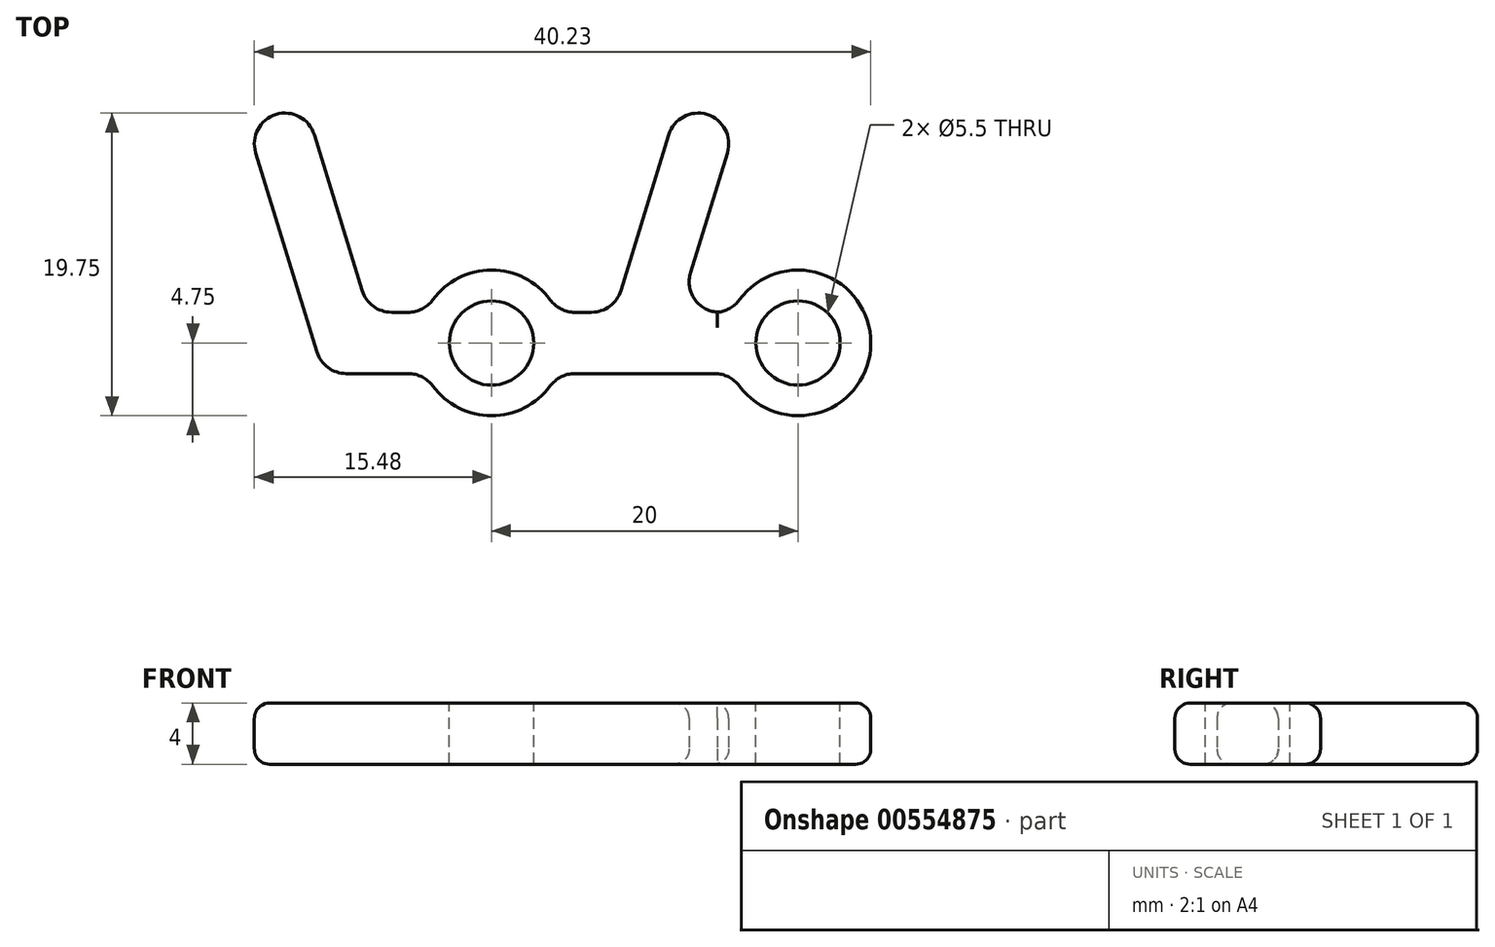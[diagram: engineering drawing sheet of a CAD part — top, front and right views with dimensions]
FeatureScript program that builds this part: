
annotation { "Feature Type Name" : "Feature", "Feature Type Description" : "" }
export const myFeature = defineFeature(function(context is Context, id is Id, definition is map)
    precondition{}
    {
        {
            var Q0;
            Q0=qCreatedBy(makeId("Top.planeOp"),FACE);
            var sketch = newSketch(context, id + "F0", { "sketchPlane" : qUnion([Q0])});
            skArc(sketch, "E0", {"start": v(-4.3, -2) * mm, "mid": v(0, -4.75) * mm, "end": v(4.3, -2) * mm});
            skLineSegment(sketch, "E1", {"start": v(4.3, -2) * mm, "end": v(10.95, -2) * mm});
            skLineSegment(sketch, "E2", {"start": v(12.19, 2) * mm, "end": v(16.19, 15) * mm});
            skLineSegment(sketch, "E3", {"start": v(16.19, 15) * mm, "end": v(12, 15) * mm});
            skLineSegment(sketch, "E4", {"start": v(12, 15) * mm, "end": v(8, 2) * mm});
            skLineSegment(sketch, "E5", {"start": v(8, 2) * mm, "end": v(4.3, 2) * mm});
            skLineSegment(sketch, "E6.MirrorCS", {"start": v(-8, 2) * mm, "end": v(-4.3, 2) * mm});
            skLineSegment(sketch, "E7.MirrorCS", {"start": v(-12, 15) * mm, "end": v(-8, 2) * mm});
            skLineSegment(sketch, "E8.MirrorCS", {"start": v(-16.19, 15) * mm, "end": v(-12, 15) * mm});
            skLineSegment(sketch, "E9.MirrorCS", {"start": v(-10.95, -2) * mm, "end": v(-16.19, 15) * mm});
            skLineSegment(sketch, "E10.MirrorCS", {"start": v(-4.3, -2) * mm, "end": v(-10.95, -2) * mm});
            skArc(sketch, "E11.trimOffspring", {"start": v(4.3, 2) * mm, "mid": v(0, 4.75) * mm, "end": v(-4.3, 2) * mm});
            skCircle(sketch, "E12", {"center": v(20, 0) * mm, "radius": 4.75 * mm});
            skLineSegment(sketch, "E13", {"start": v(12.19, 2) * mm, "end": v(15.7, 2) * mm});
            skLineSegment(sketch, "E14", {"start": v(10.95, -2) * mm, "end": v(15.7, -2) * mm});
            skSolve(sketch);
        }
        {
            var Q0;
            Q0 = qSketchRegion(id + "F0", true);
            extrude(context, id + "F1", {"entities" : qUnion([Q0]), "depth" : 4 * mm, "offsetDistance" : 25 * mm});
        }
        {
            var Q0;
            Q0=makeQuery(id+"F1.opExtrude","CAP_FACE",FACE,{"disambiguationData":[OSD([sQuery(id+"F0.wireOp",EDGE,"E0"),sQuery(id+"F0.wireOp",EDGE,"E1"),sQuery(id+"F0.wireOp",EDGE,"E2"),sQuery(id+"F0.wireOp",EDGE,"E3"),sQuery(id+"F0.wireOp",EDGE,"E4"),sQuery(id+"F0.wireOp",EDGE,"E5"),sQuery(id+"F0.wireOp",EDGE,"E6.MirrorCS"),sQuery(id+"F0.wireOp",EDGE,"E7.MirrorCS"),sQuery(id+"F0.wireOp",EDGE,"E8.MirrorCS"),sQuery(id+"F0.wireOp",EDGE,"E9.MirrorCS"),sQuery(id+"F0.wireOp",EDGE,"E10.MirrorCS"),sQuery(id+"F0.wireOp",EDGE,"E11.trimOffspring")])],"isStart":false});
            var sketch = newSketch(context, id + "F2", { "sketchPlane" : qUnion([Q0])});
            skCircle(sketch, "E15", {"center": v(0, 0) * mm, "radius": 2.75 * mm});
            skCircle(sketch, "E16", {"center": v(20, 0) * mm, "radius": 2.75 * mm});
            skSolve(sketch);
        }
        {
            var Q0;
            Q0 = qSketchRegion(id + "F2", true);
            extrude(context, id + "F3", {"entities" : qUnion([Q0]), "operationType" : NewBodyOperationType.REMOVE, "endBound" : BoundingType.THROUGH_ALL, "oppositeDirection" : true, "depth" : 25 * mm, "offsetDistance" : 25 * mm});
        }
        {
            var Q0;
            Q0=makeQuery(id+"F1.opExtrude","SWEPT_EDGE",EDGE,{"disambiguationData":[OSD([sQuery(id+"F0.wireOp",EDGE,"E8.MirrorCS"),sQuery(id+"F0.wireOp",EDGE,"E9.MirrorCS")])]});
            var Q1;
            Q1=makeQuery(id+"F1.opExtrude","SWEPT_EDGE",EDGE,{"disambiguationData":[OSD([sQuery(id+"F0.wireOp",EDGE,"E7.MirrorCS"),sQuery(id+"F0.wireOp",EDGE,"E8.MirrorCS")])]});
            var Q2;
            Q2=makeQuery(id+"F1.opExtrude","SWEPT_EDGE",EDGE,{"disambiguationData":[OSD([sQuery(id+"F0.wireOp",EDGE,"E9.MirrorCS"),sQuery(id+"F0.wireOp",EDGE,"E10.MirrorCS")])]});
            var Q3;
            Q3=makeQuery(id+"F1.opExtrude","SWEPT_EDGE",EDGE,{"disambiguationData":[OSD([sQuery(id+"F0.wireOp",EDGE,"E6.MirrorCS"),sQuery(id+"F0.wireOp",EDGE,"E11.trimOffspring")])]});
            var Q4;
            Q4=makeQuery(id+"F1.opExtrude","SWEPT_EDGE",EDGE,{"disambiguationData":[OSD([sQuery(id+"F0.wireOp",EDGE,"E6.MirrorCS"),sQuery(id+"F0.wireOp",EDGE,"E7.MirrorCS")])]});
            var Q5;
            Q5=makeQuery(id+"F1.opExtrude","SWEPT_EDGE",EDGE,{"disambiguationData":[OSD([sQuery(id+"F0.wireOp",EDGE,"E5"),sQuery(id+"F0.wireOp",EDGE,"E11.trimOffspring")])]});
            var Q6;
            Q6=makeQuery(id+"F1.opExtrude","SWEPT_EDGE",EDGE,{"disambiguationData":[OSD([sQuery(id+"F0.wireOp",EDGE,"E4"),sQuery(id+"F0.wireOp",EDGE,"E5")])]});
            var Q7;
            Q7=makeQuery(id+"F1.opExtrude","SWEPT_EDGE",EDGE,{"disambiguationData":[OSD([sQuery(id+"F0.wireOp",EDGE,"E3"),sQuery(id+"F0.wireOp",EDGE,"E4")])]});
            var Q8;
            Q8=makeQuery(id+"F1.opExtrude","SWEPT_EDGE",EDGE,{"disambiguationData":[OSD([sQuery(id+"F0.wireOp",EDGE,"E2"),sQuery(id+"F0.wireOp",EDGE,"E3")])]});
            var Q9;
            Q9=makeQuery(id+"F1.opExtrude","SWEPT_EDGE",EDGE,{"disambiguationData":[OSD([sQuery(id+"F0.wireOp",EDGE,"E1"),sQuery(id+"F0.wireOp",EDGE,"E2")])]});
            var Q10;
            Q10=makeQuery(id+"F1.opExtrude","SWEPT_EDGE",EDGE,{"disambiguationData":[OSD([sQuery(id+"F0.wireOp",EDGE,"E0"),sQuery(id+"F0.wireOp",EDGE,"E1")])]});
            var Q11;
            Q11=makeQuery(id+"F1.opExtrude","SWEPT_EDGE",EDGE,{"disambiguationData":[OSD([sQuery(id+"F0.wireOp",EDGE,"E0"),sQuery(id+"F0.wireOp",EDGE,"E10.MirrorCS")])]});
            var Q12;
            Q12=makeQuery(id+"F1.opExtrude","SWEPT_EDGE",EDGE,{"disambiguationData":[OSD([sQuery(id+"F0.wireOp",EDGE,"E12"),sQuery(id+"F0.wireOp",EDGE,"E13")])]});
            var Q13;
            Q13=makeQuery(id+"F1.opExtrude","SWEPT_EDGE",EDGE,{"disambiguationData":[OSD([sQuery(id+"F0.wireOp",EDGE,"E12"),sQuery(id+"F0.wireOp",EDGE,"E14")])]});
            fillet(context, id + "F4", {"entities" : qUnion([Q0, Q1, Q2, Q3, Q4, Q5, Q6, Q7, Q8, Q9, Q10, Q11, Q12, Q13]), "radius" : 2 * mm, "tangentPropagation" : true, "allowEdgeOverflow" : false});
        }
        {
            var Q0;
            Q0=makeQuery(id+"F1.opExtrude","CAP_EDGE",EDGE,{"disambiguationData":[OSD([sQuery(id+"F0.wireOp",EDGE,"E2")])],"isStart":false});
            var Q1;
            Q1=makeQuery(id+"F1.opExtrude","CAP_EDGE",EDGE,{"disambiguationData":[OSD([sQuery(id+"F0.wireOp",EDGE,"E1")])],"isStart":true});
            fillet(context, id + "F5", {"entities" : qUnion([Q0, Q1]), "radius" : 1 * mm, "tangentPropagation" : true, "allowEdgeOverflow" : false});
        }
    });
